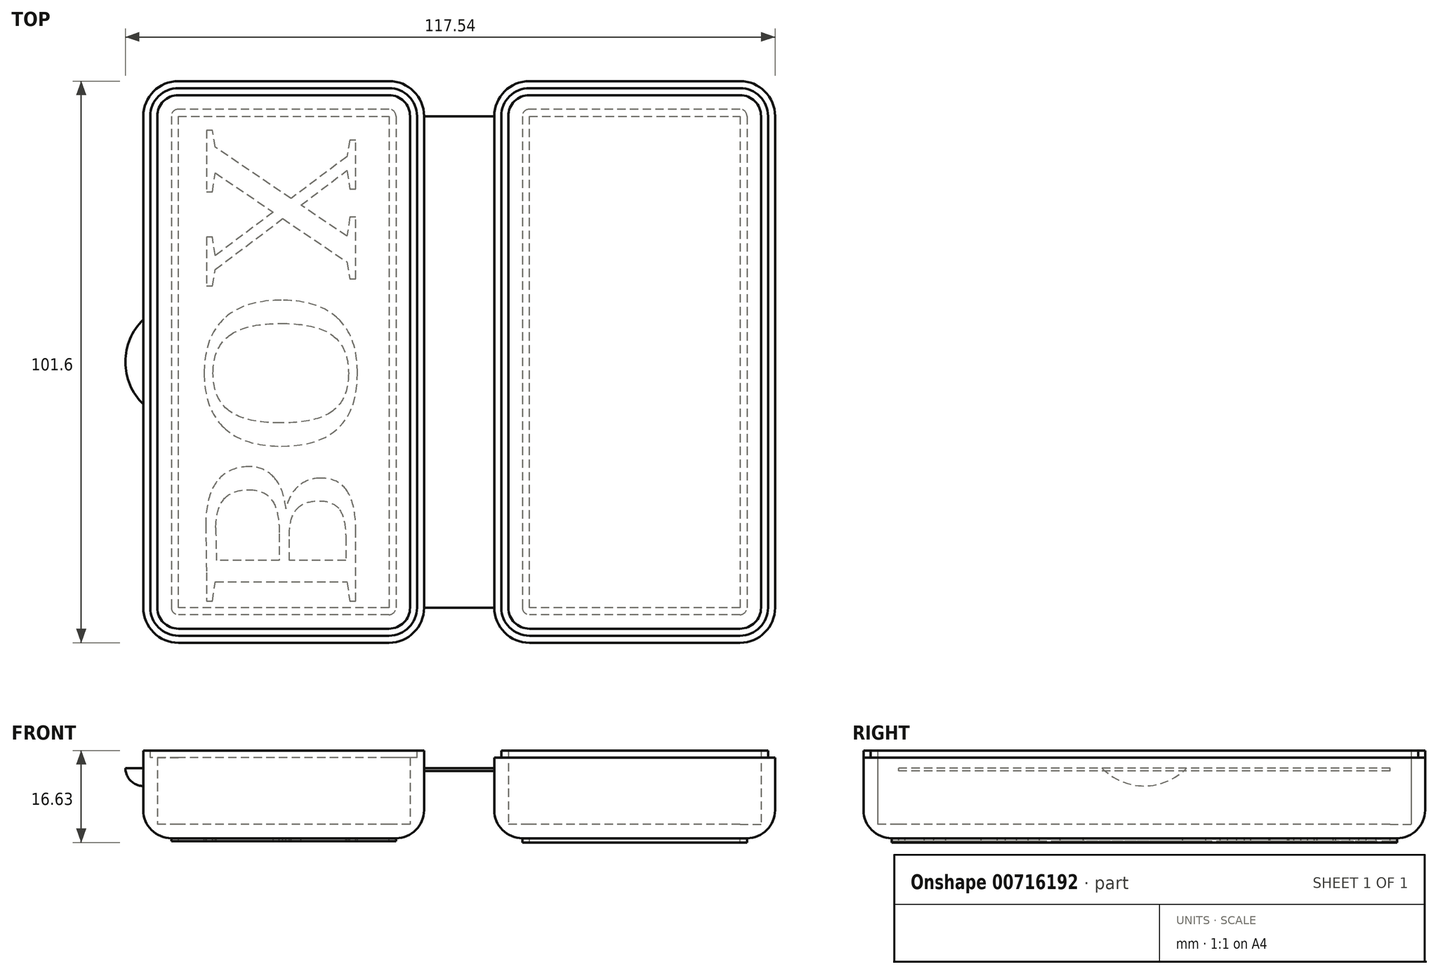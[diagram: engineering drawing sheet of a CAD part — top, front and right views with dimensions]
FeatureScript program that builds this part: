
annotation { "Feature Type Name" : "Feature", "Feature Type Description" : "" }
export const myFeature = defineFeature(function(context is Context, id is Id, definition is map)
    precondition{}
    {
        {
            var Q0;
            Q0=qCreatedBy(makeId("Top.planeOp"),FACE);
            var sketch = newSketch(context, id + "F0", { "sketchPlane" : qUnion([Q0])});
            skLineSegment(sketch, "E0.bottom", {"start": v(50.8, 50.8) * mm, "end": v(12.7, 50.8) * mm});
            skLineSegment(sketch, "E0.top", {"start": v(50.8, -50.8) * mm, "end": v(12.7, -50.8) * mm});
            skLineSegment(sketch, "E0.left", {"start": v(57.15, 44.45) * mm, "end": v(57.15, -44.45) * mm});
            skLineSegment(sketch, "E0.right", {"start": v(-57.15, 44.45) * mm, "end": v(-57.15, -44.45) * mm});
            skPoint(sketch, "E0.middle", {"position": v(0, 0) * mm});
            skLineSegment(sketch, "E1", {"start": v(0, 50.8) * mm, "end": v(0, -50.8) * mm, "construction": true});
            skLineSegment(sketch, "E2", {"start": v(-6.35, 44.45) * mm, "end": v(-6.35, -44.45) * mm});
            skLineSegment(sketch, "E3", {"start": v(6.35, 44.45) * mm, "end": v(6.35, -44.45) * mm});
            skLineSegment(sketch, "E4", {"start": v(-6.35, 44.45) * mm, "end": v(6.35, 44.45) * mm});
            skLineSegment(sketch, "E5", {"start": v(-6.35, -44.45) * mm, "end": v(6.35, -44.45) * mm});
            skLineSegment(sketch, "E6.trimOffspring", {"start": v(-12.7, 50.8) * mm, "end": v(-50.8, 50.8) * mm});
            skLineSegment(sketch, "E7.trimOffspring", {"start": v(-12.7, -50.8) * mm, "end": v(-50.8, -50.8) * mm});
            skPoint(sketch, "E8.visualSharp", {"position": v(-57.15, 50.8) * mm});
            skArc(sketch, "E8.filletArc", {"start": v(-50.8, 50.8) * mm, "mid": v(-55.3, 48.94) * mm, "end": v(-57.15, 44.45) * mm});
            skPoint(sketch, "E9.visualSharp", {"position": v(-57.15, -50.8) * mm});
            skArc(sketch, "E9.filletArc", {"start": v(-57.15, -44.45) * mm, "mid": v(-55.3, -48.94) * mm, "end": v(-50.8, -50.8) * mm});
            skPoint(sketch, "E10.visualSharp", {"position": v(-6.35, -50.8) * mm});
            skArc(sketch, "E10.filletArc", {"start": v(-12.7, -50.8) * mm, "mid": v(-8.2, -48.94) * mm, "end": v(-6.35, -44.45) * mm});
            skPoint(sketch, "E11.visualSharp", {"position": v(57.15, -50.8) * mm});
            skArc(sketch, "E11.filletArc", {"start": v(50.8, -50.8) * mm, "mid": v(55.3, -48.94) * mm, "end": v(57.15, -44.45) * mm});
            skPoint(sketch, "E12.visualSharp", {"position": v(57.15, 50.8) * mm});
            skArc(sketch, "E12.filletArc", {"start": v(57.15, 44.45) * mm, "mid": v(55.3, 48.94) * mm, "end": v(50.8, 50.8) * mm});
            skPoint(sketch, "E13.visualSharp", {"position": v(6.35, 50.8) * mm});
            skArc(sketch, "E13.filletArc", {"start": v(12.7, 50.8) * mm, "mid": v(8.2, 48.94) * mm, "end": v(6.35, 44.45) * mm});
            skPoint(sketch, "E14.visualSharp", {"position": v(-6.35, 50.8) * mm});
            skArc(sketch, "E14.filletArc", {"start": v(-6.35, 44.45) * mm, "mid": v(-8.2, 48.94) * mm, "end": v(-12.7, 50.8) * mm});
            skPoint(sketch, "E15.visualSharp", {"position": v(6.35, -50.8) * mm});
            skArc(sketch, "E15.filletArc", {"start": v(6.35, -44.45) * mm, "mid": v(8.2, -48.94) * mm, "end": v(12.7, -50.8) * mm});
            skArc(sketch, "E16", {"start": v(-57.15, 7.65) * mm, "mid": v(-60.39, 0) * mm, "end": v(-57.15, -7.65) * mm});
            skSolve(sketch);
        }
        {
            var Q0;
            Q0=makeQuery(id+"F0.imprint","IMPRINT",FACE,{"disambiguationData":[TD([[makeQuery(id+"F0.imprint","IMPRINT",EDGE,{"derivedFrom":sQuery(id+"F0.wireOp",EDGE,"E0.right")}),1.0]])]});
            var Q1;
            {var subQ1=sQuery(id+"F0.wireOp",EDGE,"E0.bottom");Q1=makeQuery(id+"F0.imprint","IMPRINT",FACE,{"disambiguationData":[TD([[makeQuery(id+"F0.imprint","IMPRINT",EDGE,{"derivedFrom":subQ1}),1.0]])]});}
            extrude(context, id + "F1", {"entities" : qUnion([Q0, Q1]), "depth" : 3.17 * mm, "offsetDistance" : 25.4 * mm, "hasSecondDirection" : true, "secondDirectionOppositeDirection" : true, "secondDirectionDepth" : 12.7 * mm});
        }
        {
            var Q0;
            {var subQ0=sQuery(id+"F0.wireOp",EDGE,"E4");Q0=makeQuery(id+"F0.imprint","IMPRINT",FACE,{"disambiguationData":[TD([[makeQuery(id+"F0.imprint","IMPRINT",EDGE,{"derivedFrom":subQ0}),-1.0]])]});}
            extrude(context, id + "F2", {"entities" : qUnion([Q0]), "operationType" : NewBodyOperationType.ADD, "oppositeDirection" : true, "depth" : 0.5 * mm, "offsetDistance" : 25.4 * mm});
        }
        {
            var Q0;
            Q0=makeQuery(id+"F1.opExtrude","CAP_FACE",FACE,{"disambiguationData":[OSD([sQuery(id+"F0.wireOp",EDGE,"E0.right"),sQuery(id+"F0.wireOp",EDGE,"E2"),sQuery(id+"F0.wireOp",EDGE,"E6.trimOffspring"),sQuery(id+"F0.wireOp",EDGE,"E7.trimOffspring")])],"isStart":false});
            var Q1;
            Q1=makeQuery(id+"F1.opExtrude","CAP_FACE",FACE,{"disambiguationData":[OSD([sQuery(id+"F0.wireOp",EDGE,"E0.bottom"),sQuery(id+"F0.wireOp",EDGE,"E0.top"),sQuery(id+"F0.wireOp",EDGE,"E0.left"),sQuery(id+"F0.wireOp",EDGE,"E3")])],"isStart":false});
            shell(context, id + "F3", {"entities" : qUnion([Q0, Q1]), "thickness" : 2.54 * mm});
        }
        {
            var Q0;
            Q0=makeQuery(id+"F1.opExtrude","CAP_FACE",FACE,{"disambiguationData":[OSD([sQuery(id+"F0.wireOp",EDGE,"E0.right"),sQuery(id+"F0.wireOp",EDGE,"E2"),sQuery(id+"F0.wireOp",EDGE,"E6.trimOffspring"),sQuery(id+"F0.wireOp",EDGE,"E7.trimOffspring")])],"isStart":false});
            var sketch = newSketch(context, id + "F4", { "sketchPlane" : qUnion([Q0])});
            skLineSegment(sketch, "E17.0", {"start": v(-12.7, 49.53) * mm, "end": v(-50.8, 49.53) * mm});
            skLineSegment(sketch, "E17.1", {"start": v(-7.62, 44.45) * mm, "end": v(-7.62, -44.45) * mm});
            skLineSegment(sketch, "E17.2", {"start": v(-12.7, -49.53) * mm, "end": v(-50.8, -49.53) * mm});
            skLineSegment(sketch, "E17.3", {"start": v(-55.88, 44.45) * mm, "end": v(-55.88, -44.45) * mm});
            skPoint(sketch, "E18.visualSharp", {"position": v(-55.88, 49.53) * mm});
            skArc(sketch, "E18.filletArc", {"start": v(-50.8, 49.53) * mm, "mid": v(-54.4, 48.04) * mm, "end": v(-55.88, 44.45) * mm});
            skPoint(sketch, "E19.visualSharp", {"position": v(-7.62, 49.53) * mm});
            skArc(sketch, "E19.filletArc", {"start": v(-7.62, 44.45) * mm, "mid": v(-9.1, 48.04) * mm, "end": v(-12.7, 49.53) * mm});
            skPoint(sketch, "E20.visualSharp", {"position": v(-7.62, -49.53) * mm});
            skArc(sketch, "E20.filletArc", {"start": v(-12.7, -49.53) * mm, "mid": v(-9.1, -48.04) * mm, "end": v(-7.62, -44.45) * mm});
            skPoint(sketch, "E21.visualSharp", {"position": v(-55.88, -49.53) * mm});
            skArc(sketch, "E21.filletArc", {"start": v(-55.88, -44.45) * mm, "mid": v(-54.4, -48.04) * mm, "end": v(-50.8, -49.53) * mm});
            skSolve(sketch);
        }
        {
            var Q0;
            Q0=makeQuery(id+"F4.imprint","IMPRINT",FACE,{"disambiguationData":[TD([[makeQuery(id+"F4.imprint","IMPRINT",EDGE,{"derivedFrom":sQuery(id+"F4.wireOp",EDGE,"E17.0")}),1.0]])]});
            extrude(context, id + "F5", {"entities" : qUnion([Q0]), "operationType" : NewBodyOperationType.REMOVE, "oppositeDirection" : true, "depth" : 1.27 * mm, "offsetDistance" : 25.4 * mm});
        }
        {
            var Q0;
            Q0=makeQuery(id+"F1.opExtrude","CAP_FACE",FACE,{"disambiguationData":[OSD([sQuery(id+"F0.wireOp",EDGE,"E0.bottom"),sQuery(id+"F0.wireOp",EDGE,"E0.top"),sQuery(id+"F0.wireOp",EDGE,"E0.left"),sQuery(id+"F0.wireOp",EDGE,"E3")])],"isStart":false});
            var sketch = newSketch(context, id + "F6", { "sketchPlane" : qUnion([Q0])});
            skLineSegment(sketch, "E22.0", {"start": v(50.8, -49.53) * mm, "end": v(12.7, -49.53) * mm});
            skLineSegment(sketch, "E22.1", {"start": v(55.88, 44.45) * mm, "end": v(55.88, -44.45) * mm});
            skLineSegment(sketch, "E22.2", {"start": v(50.8, 49.53) * mm, "end": v(12.7, 49.53) * mm});
            skLineSegment(sketch, "E22.3", {"start": v(7.62, 44.45) * mm, "end": v(7.62, -44.45) * mm});
            skPoint(sketch, "E23.visualSharp", {"position": v(7.62, 49.53) * mm});
            skArc(sketch, "E23.filletArc", {"start": v(12.7, 49.53) * mm, "mid": v(9.1, 48.04) * mm, "end": v(7.62, 44.45) * mm});
            skPoint(sketch, "E24.visualSharp", {"position": v(55.88, 49.53) * mm});
            skArc(sketch, "E24.filletArc", {"start": v(55.88, 44.45) * mm, "mid": v(54.4, 48.04) * mm, "end": v(50.8, 49.53) * mm});
            skPoint(sketch, "E25.visualSharp", {"position": v(7.62, -49.53) * mm});
            skArc(sketch, "E25.filletArc", {"start": v(7.62, -44.45) * mm, "mid": v(9.1, -48.04) * mm, "end": v(12.7, -49.53) * mm});
            skPoint(sketch, "E26.visualSharp", {"position": v(55.88, -49.53) * mm});
            skArc(sketch, "E26.filletArc", {"start": v(50.8, -49.53) * mm, "mid": v(54.4, -48.04) * mm, "end": v(55.88, -44.45) * mm});
            skSolve(sketch);
        }
        {
            var Q0;
            Q0=makeQuery(id+"F6.imprint","IMPRINT",FACE,{"disambiguationData":[TD([[makeQuery(id+"F6.imprint","IMPRINT",EDGE,{"derivedFrom":sQuery(id+"F6.wireOp",EDGE,"E22.0")}),1.0]])]});
            extrude(context, id + "F7", {"entities" : qUnion([Q0]), "operationType" : NewBodyOperationType.REMOVE, "oppositeDirection" : true, "depth" : 1.27 * mm, "offsetDistance" : 25.4 * mm});
        }
        {
            var Q0;
            {var subQ0=sQuery(id+"F0.wireOp",EDGE,"E16");Q0=makeQuery(id+"F0.imprint","IMPRINT",FACE,{"disambiguationData":[TD([[makeQuery(id+"F0.imprint","IMPRINT",EDGE,{"derivedFrom":subQ0}),1.0]])]});}
            var Q1;
            Q1=sQuery(id+"F0.wireOp",EDGE,"E0.right");
            revolve(context, id + "F8", {"operationType" : NewBodyOperationType.ADD, "surfaceOperationType" : NewSurfaceOperationType.NEW, "entities" : qUnion([Q0]), "axis" : qUnion([Q1]), "revolveType" : RevolveType.ONE_DIRECTION, "angle" : 90 * degree});
        }
        {
            var Q0;
            Q0=makeQuery(id+"F1.opExtrude","CAP_FACE",FACE,{"disambiguationData":[OSD([sQuery(id+"F0.wireOp",EDGE,"E0.bottom"),sQuery(id+"F0.wireOp",EDGE,"E0.top"),sQuery(id+"F0.wireOp",EDGE,"E0.left"),sQuery(id+"F0.wireOp",EDGE,"E3"),sQuery(id+"F0.wireOp",EDGE,"E11.filletArc"),sQuery(id+"F0.wireOp",EDGE,"E12.filletArc"),sQuery(id+"F0.wireOp",EDGE,"E13.filletArc"),sQuery(id+"F0.wireOp",EDGE,"E15.filletArc")])],"isStart":true});
            var Q1;
            Q1=makeQuery(id+"F1.opExtrude","CAP_FACE",FACE,{"disambiguationData":[OSD([sQuery(id+"F0.wireOp",EDGE,"E0.right"),sQuery(id+"F0.wireOp",EDGE,"E2"),sQuery(id+"F0.wireOp",EDGE,"E6.trimOffspring"),sQuery(id+"F0.wireOp",EDGE,"E7.trimOffspring"),sQuery(id+"F0.wireOp",EDGE,"E8.filletArc"),sQuery(id+"F0.wireOp",EDGE,"E9.filletArc"),sQuery(id+"F0.wireOp",EDGE,"E10.filletArc"),sQuery(id+"F0.wireOp",EDGE,"E14.filletArc")])],"isStart":true});
            fillet(context, id + "F9", {"entities" : qUnion([Q0, Q1]), "radius" : 5.08 * mm, "tangentPropagation" : true, "allowEdgeOverflow" : false});
        }
        {
            var Q0;
            Q0=makeQuery(id+"F1.opExtrude","CAP_FACE",FACE,{"disambiguationData":[OSD([sQuery(id+"F0.wireOp",EDGE,"E0.bottom"),sQuery(id+"F0.wireOp",EDGE,"E0.top"),sQuery(id+"F0.wireOp",EDGE,"E0.left"),sQuery(id+"F0.wireOp",EDGE,"E3"),sQuery(id+"F0.wireOp",EDGE,"E11.filletArc"),sQuery(id+"F0.wireOp",EDGE,"E12.filletArc"),sQuery(id+"F0.wireOp",EDGE,"E13.filletArc"),sQuery(id+"F0.wireOp",EDGE,"E15.filletArc")])],"isStart":true});
            var sketch = newSketch(context, id + "F10", { "sketchPlane" : qUnion([Q0])});
            skLineSegment(sketch, "E27.0", {"start": v(50.8, 44.45) * mm, "end": v(12.7, 44.45) * mm});
            skLineSegment(sketch, "E27.1", {"start": v(50.8, -44.45) * mm, "end": v(50.8, 44.45) * mm});
            skLineSegment(sketch, "E27.2", {"start": v(12.7, -44.45) * mm, "end": v(50.8, -44.45) * mm});
            skLineSegment(sketch, "E27.3", {"start": v(12.7, 44.45) * mm, "end": v(12.7, -44.45) * mm});
            skSolve(sketch);
        }
        {
            var Q0;
            Q0=makeQuery(id+"F10.imprint","IMPRINT",FACE,{"disambiguationData":[TD([[makeQuery(id+"F10.imprint","IMPRINT",EDGE,{"derivedFrom":sQuery(id+"F10.wireOp",EDGE,"E27.0")}),-1.0]])]});
            extrude(context, id + "F11", {"entities" : qUnion([Q0]), "operationType" : NewBodyOperationType.ADD, "depth" : 0.76 * mm, "offsetDistance" : 25.4 * mm});
        }
        {
            var Q0;
            Q0=makeQuery(id+"F1.opExtrude","CAP_FACE",FACE,{"disambiguationData":[OSD([sQuery(id+"F0.wireOp",EDGE,"E0.right"),sQuery(id+"F0.wireOp",EDGE,"E2"),sQuery(id+"F0.wireOp",EDGE,"E6.trimOffspring"),sQuery(id+"F0.wireOp",EDGE,"E7.trimOffspring"),sQuery(id+"F0.wireOp",EDGE,"E8.filletArc"),sQuery(id+"F0.wireOp",EDGE,"E9.filletArc"),sQuery(id+"F0.wireOp",EDGE,"E10.filletArc"),sQuery(id+"F0.wireOp",EDGE,"E14.filletArc")])],"isStart":true});
            var sketch = newSketch(context, id + "F12", { "sketchPlane" : qUnion([Q0])});
            skLineSegment(sketch, "E28.0", {"start": v(-12.7, 44.45) * mm, "end": v(-50.8, 44.45) * mm});
            skLineSegment(sketch, "E28.1", {"start": v(-12.7, -44.45) * mm, "end": v(-12.7, 44.45) * mm});
            skLineSegment(sketch, "E28.2", {"start": v(-50.8, -44.45) * mm, "end": v(-12.7, -44.45) * mm});
            skLineSegment(sketch, "E28.3", {"start": v(-50.8, 44.45) * mm, "end": v(-50.8, -44.45) * mm});
            skText(sketch, "E29", { "text": "BOX", "fontName": "Tinos-Regular.ttf"});
            const initialGuessF12  = {"E29": [-0.04572, 0.04445, 0, -1, 0.0297]};
            skSetInitialGuess(sketch, initialGuessF12);
            skSolve(sketch);
        }
        {
            var Q0;
            Q0=makeQuery(id+"F12.imprint","IMPRINT",FACE,{"disambiguationData":[TD([[makeQuery(id+"F12.imprint","IMPRINT",EDGE,{"derivedFrom":sQuery(id+"F12.wireOp",EDGE,"E28.0")}),-1.0]])]});
            var Q1;
            Q1=makeQuery(id+"F12.imprint","IMPRINT",FACE,{"disambiguationData":[TD([[makeQuery(id+"F12.imprint","IMPRINT",EDGE,{"derivedFrom":sQuery(id+"F12.wireOp",EDGE,"E29.sketch_text.stroke-0")}),-1.0]])]});
            var Q2;
            Q2=makeQuery(id+"F12.imprint","IMPRINT",FACE,{"disambiguationData":[TD([[makeQuery(id+"F12.imprint","IMPRINT",EDGE,{"derivedFrom":sQuery(id+"F12.wireOp",EDGE,"E29.sketch_text.stroke-30")}),-1.0]])]});
            var Q3;
            Q3=makeQuery(id+"F12.imprint","IMPRINT",FACE,{"disambiguationData":[TD([[makeQuery(id+"F12.imprint","IMPRINT",EDGE,{"derivedFrom":sQuery(id+"F12.wireOp",EDGE,"E29.sketch_text.stroke-45")}),-1.0]])]});
            extrude(context, id + "F13", {"entities" : qUnion([Q0, Q1, Q2, Q3]), "operationType" : NewBodyOperationType.ADD, "depth" : 0.5 * mm, "offsetDistance" : 25.4 * mm});
        }
    });
